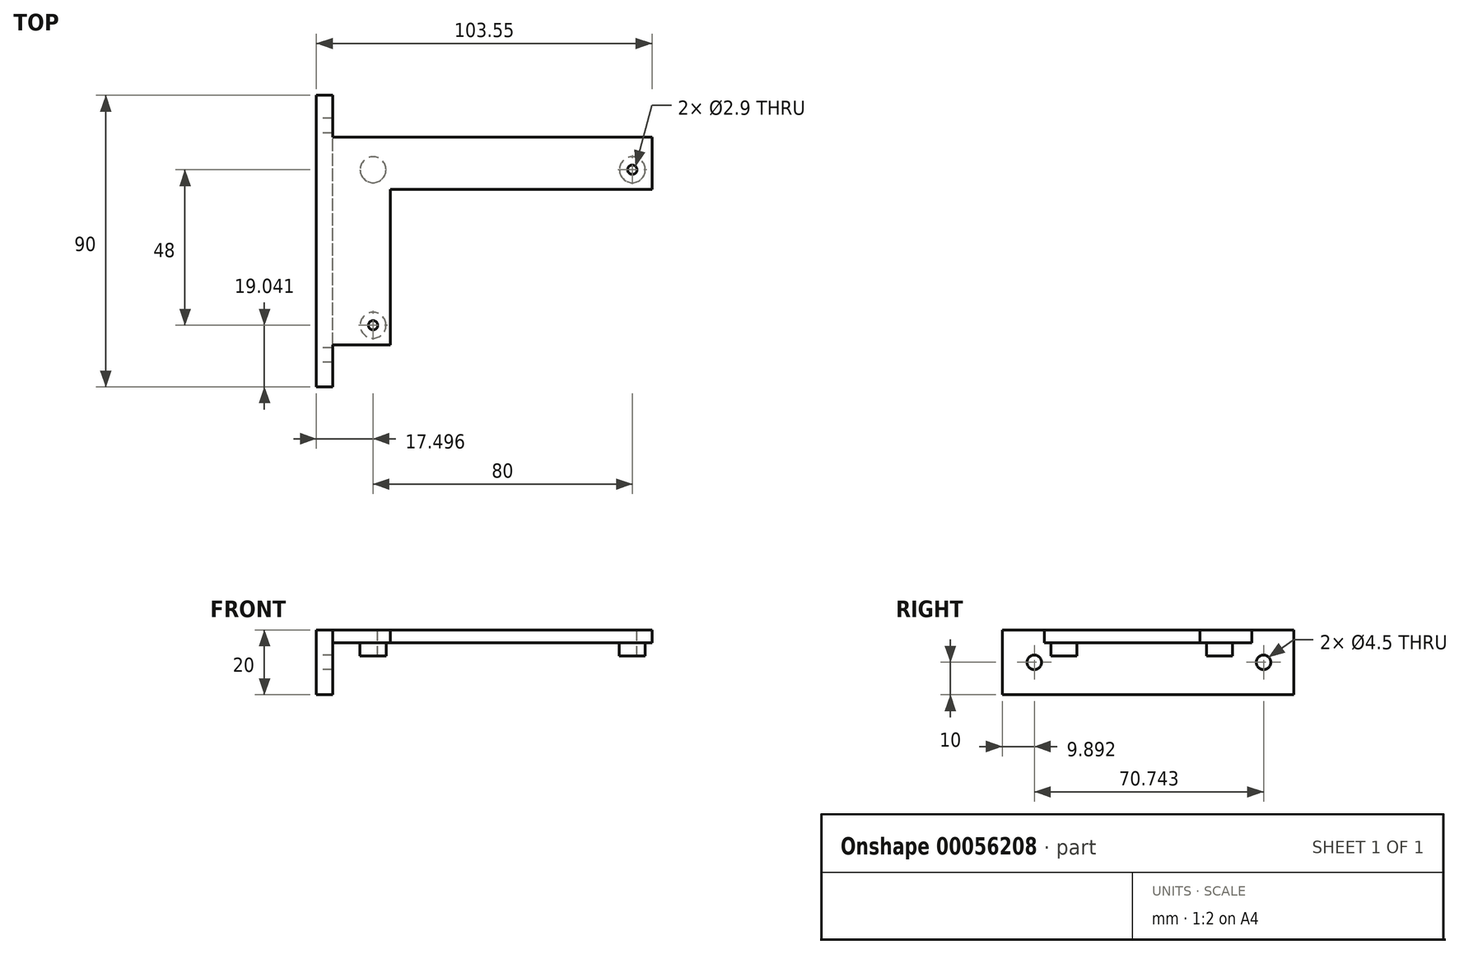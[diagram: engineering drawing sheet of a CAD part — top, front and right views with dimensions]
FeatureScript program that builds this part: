
annotation { "Feature Type Name" : "Feature", "Feature Type Description" : "" }
export const myFeature = defineFeature(function(context is Context, id is Id, definition is map)
    precondition{}
    {
        {
            var Q0;
            Q0=qCreatedBy(makeId("Top.planeOp"),FACE);
            var sketch = newSketch(context, id + "F0", { "sketchPlane" : qUnion([Q0])});
            skLineSegment(sketch, "E0.bottom", {"start": v(-70.88, 32.6) * mm, "end": v(32.67, 32.6) * mm});
            skLineSegment(sketch, "E0.left", {"start": v(-70.88, 32.6) * mm, "end": v(-70.88, -31.48) * mm});
            skLineSegment(sketch, "E1", {"start": v(32.67, 16.5) * mm, "end": v(-48.08, 16.5) * mm});
            skLineSegment(sketch, "E2", {"start": v(-48.08, 16.5) * mm, "end": v(-48.08, -31.48) * mm});
            skLineSegment(sketch, "E3", {"start": v(32.67, 16.5) * mm, "end": v(32.67, 32.6) * mm});
            skLineSegment(sketch, "E4", {"start": v(-70.88, -31.48) * mm, "end": v(-48.08, -31.48) * mm});
            skSolve(sketch);
        }
        {
            var Q0;
            Q0=qSketchRegion(id+"F0",true);
            extrude(context, id + "F1", {"entities" : qUnion([Q0]), "oppositeDirection" : true, "depth" : 4 * mm});
        }
        {
            var Q0;
            Q0=makeQuery(id+"F1.opExtrude","CAP_FACE",FACE,{"disambiguationData":[OSD([sQuery(id+"F0.wireOp",EDGE,"E0.bottom"),sQuery(id+"F0.wireOp",EDGE,"E0.left"),sQuery(id+"F0.wireOp",EDGE,"E1"),sQuery(id+"F0.wireOp",EDGE,"E2"),sQuery(id+"F0.wireOp",EDGE,"E3"),sQuery(id+"F0.wireOp",EDGE,"E4")])],"isStart":false});
            var sketch = newSketch(context, id + "F2", { "sketchPlane" : qUnion([Q0])});
            skCircle(sketch, "E5", {"center": v(-53.38, 25.4) * mm, "radius": 4 * mm});
            skCircle(sketch, "E6", {"center": v(26.62, -22.6) * mm, "radius": 4 * mm});
            skCircle(sketch, "E7", {"center": v(-53.38, 25.4) * mm, "radius": 1.45 * mm});
            skCircle(sketch, "E8", {"center": v(26.62, -22.6) * mm, "radius": 1.45 * mm});
            skLineSegment(sketch, "E9", {"start": v(-65.88, 31.48) * mm, "end": v(-65.88, -32.6) * mm});
            skLineSegment(sketch, "E10.bottom", {"start": v(-70.88, 31.48) * mm, "end": v(-65.88, 31.48) * mm});
            skLineSegment(sketch, "E10.top", {"start": v(-70.88, 44.44) * mm, "end": v(-65.88, 44.44) * mm});
            skLineSegment(sketch, "E10.left", {"start": v(-70.88, 31.48) * mm, "end": v(-70.88, 44.44) * mm});
            skLineSegment(sketch, "E10.right", {"start": v(-65.88, 31.48) * mm, "end": v(-65.88, 44.44) * mm});
            skLineSegment(sketch, "E11.bottom", {"start": v(-70.88, -32.6) * mm, "end": v(-65.88, -32.6) * mm});
            skLineSegment(sketch, "E11.top", {"start": v(-70.88, -45.56) * mm, "end": v(-65.88, -45.56) * mm});
            skLineSegment(sketch, "E11.left", {"start": v(-70.88, -32.6) * mm, "end": v(-70.88, -45.56) * mm});
            skLineSegment(sketch, "E11.right", {"start": v(-65.88, -32.6) * mm, "end": v(-65.88, -45.56) * mm});
            skCircle(sketch, "E12", {"center": v(-53.38, -22.6) * mm, "radius": 4 * mm});
            skSolve(sketch);
        }
        {
            var Q0;
            Q0=makeQuery(id+"F2.imprint","IMPRINT",FACE,{"disambiguationData":[TD([[makeQuery(id+"F2.imprint","IMPRINT",EDGE,{"derivedFrom":sQuery(id+"F2.wireOp",EDGE,"E5")}),1.0]])]});
            var Q1;
            Q1=makeQuery(id+"F2.imprint","IMPRINT",FACE,{"disambiguationData":[TD([[makeQuery(id+"F2.imprint","IMPRINT",EDGE,{"derivedFrom":sQuery(id+"F2.wireOp",EDGE,"E6")}),1.0]])]});
            var Q2;
            Q2=makeQuery(id+"F2.imprint","IMPRINT",FACE,{"disambiguationData":[TD([[makeQuery(id+"F2.imprint","IMPRINT",EDGE,{"derivedFrom":sQuery(id+"F2.wireOp",EDGE,"E12")}),1.0]])]});
            extrude(context, id + "F3", {"entities" : qUnion([Q0, Q1, Q2]), "operationType" : NewBodyOperationType.ADD, "depth" : 4 * mm});
        }
        {
            var Q0;
            {var subQ1=sQuery(id+"F2.wireOp",EDGE,"E9");Q0=makeQuery(id+"F2.imprint","IMPRINT",FACE,{"disambiguationData":[TD([[makeQuery(id+"F2.imprint","IMPRINT",EDGE,{"derivedFrom":subQ1}),-1.0]])]});}
            var Q1;
            Q1=makeQuery(id+"F2.imprint","IMPRINT",FACE,{"disambiguationData":[TD([[makeQuery(id+"F2.imprint","IMPRINT",EDGE,{"derivedFrom":sQuery(id+"F2.wireOp",EDGE,"E10.bottom")}),1.0]])]});
            var Q2;
            Q2=makeQuery(id+"F2.imprint","IMPRINT",FACE,{"disambiguationData":[TD([[makeQuery(id+"F2.imprint","IMPRINT",EDGE,{"derivedFrom":sQuery(id+"F2.wireOp",EDGE,"E11.bottom")}),-1.0]])]});
            extrude(context, id + "F4", {"entities" : qUnion([Q0, Q1, Q2]), "operationType" : NewBodyOperationType.ADD, "depth" : 16 * mm});
        }
        {
            var Q0;
            {var subQ0=sQuery(id+"F0.wireOp",EDGE,"E0.left");Q0=makeQuery(id+"F4.boolean.opBoolean","MERGE",FACE,{"derivedFrom":[makeQuery(id+"F1.opExtrude","SWEPT_FACE",FACE,{"disambiguationData":[OSD([subQ0])]}),makeQuery(id+"F4.opExtrude","SWEPT_FACE",FACE,{"disambiguationData":[OSD([subQ0])]})]});}
            var sketch = newSketch(context, id + "F5", { "sketchPlane" : qUnion([Q0])});
            skLineSegment(sketch, "E13", {"start": v(-33.38, -10) * mm, "end": v(30.7, -10) * mm, "construction": true});
            skCircle(sketch, "E14", {"center": v(-36.2, -10) * mm, "radius": 2.25 * mm});
            skCircle(sketch, "E15", {"center": v(34.55, -10) * mm, "radius": 2.25 * mm});
            skSolve(sketch);
        }
        {
            var Q0;
            Q0=qSketchRegion(id+"F5",true);
            extrude(context, id + "F6", {"entities" : qUnion([Q0]), "operationType" : NewBodyOperationType.REMOVE, "oppositeDirection" : true, "depth" : 25 * mm});
        }
        {
            var Q0;
            Q0=makeQuery(id+"F2.imprint","IMPRINT",FACE,{"disambiguationData":[TD([[makeQuery(id+"F2.imprint","IMPRINT",EDGE,{"derivedFrom":sQuery(id+"F2.wireOp",EDGE,"E10.bottom")}),1.0]])]});
            var Q1;
            Q1=makeQuery(id+"F2.imprint","IMPRINT",FACE,{"disambiguationData":[TD([[makeQuery(id+"F2.imprint","IMPRINT",EDGE,{"derivedFrom":sQuery(id+"F2.wireOp",EDGE,"E11.bottom")}),-1.0]])]});
            extrude(context, id + "F7", {"entities" : qUnion([Q0, Q1]), "operationType" : NewBodyOperationType.ADD, "oppositeDirection" : true, "depth" : 4 * mm});
        }
        {
            var Q0;
            Q0=makeQuery(id+"F2.imprint","IMPRINT",FACE,{"disambiguationData":[TD([[makeQuery(id+"F2.imprint","IMPRINT",EDGE,{"derivedFrom":sQuery(id+"F2.wireOp",EDGE,"E7")}),1.0]])]});
            var Q1;
            Q1=makeQuery(id+"F2.imprint","IMPRINT",FACE,{"disambiguationData":[TD([[makeQuery(id+"F2.imprint","IMPRINT",EDGE,{"derivedFrom":sQuery(id+"F2.wireOp",EDGE,"E8")}),1.0]])]});
            extrude(context, id + "F8", {"entities" : qUnion([Q0, Q1]), "operationType" : NewBodyOperationType.REMOVE, "oppositeDirection" : true, "depth" : 25 * mm});
        }
    });
